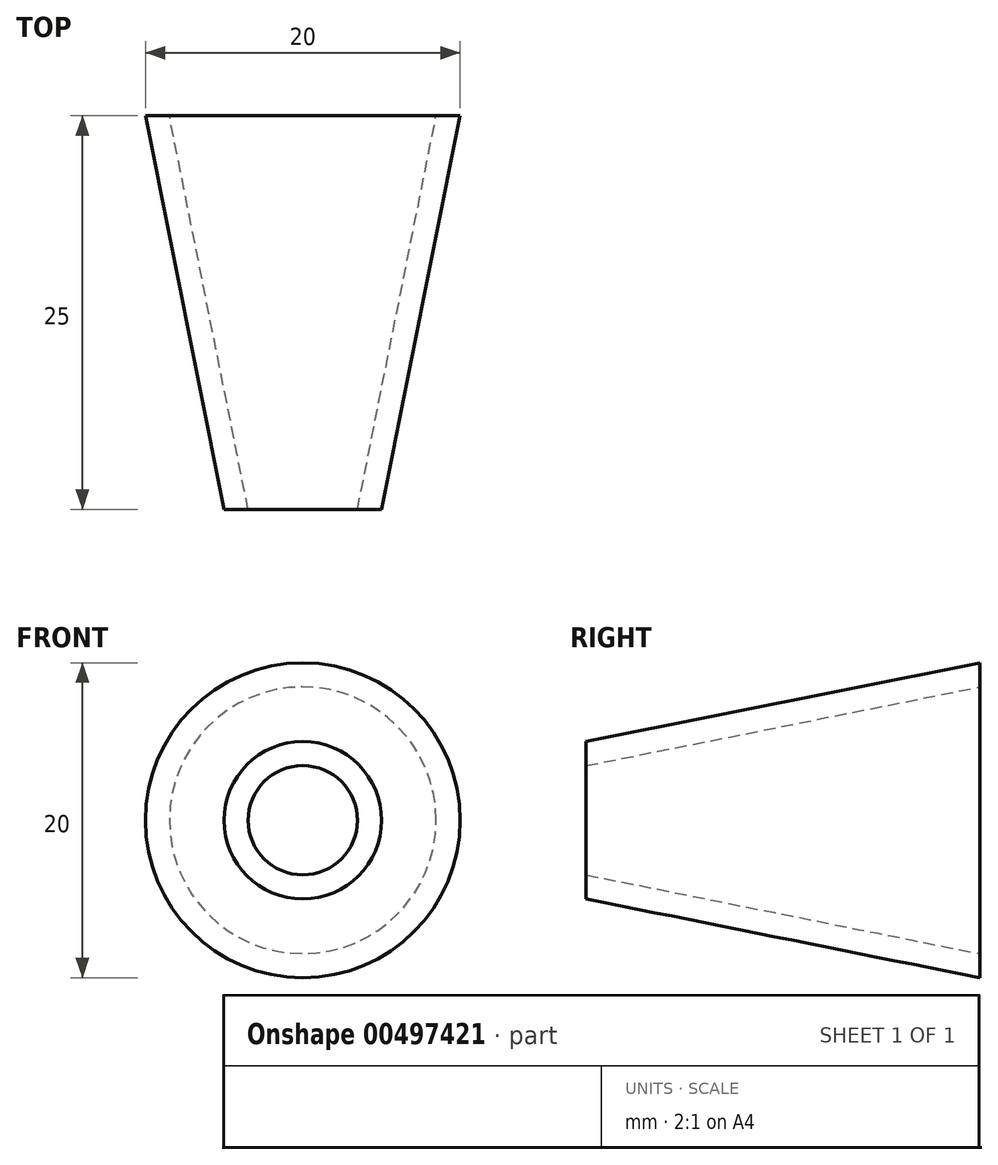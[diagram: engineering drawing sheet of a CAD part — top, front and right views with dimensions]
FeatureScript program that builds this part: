
annotation { "Feature Type Name" : "Feature", "Feature Type Description" : "" }
export const myFeature = defineFeature(function(context is Context, id is Id, definition is map)
    precondition{}
    {
        {
            var Q0;
            Q0=qCreatedBy(makeId("Front.planeOp"),FACE);
            var sketch = newSketch(context, id + "F0", { "sketchPlane" : qUnion([Q0])});
            skCircle(sketch, "E0", {"center": v(0, 0) * mm, "radius": 10 * mm});
            skSolve(sketch);
        }
        {
            var Q0;
            Q0 = qSketchRegion(id + "F0", true);
            extrude(context, id + "F1", {"entities" : qUnion([Q0]), "depth" : 25 * mm});
        }
        {
            var Q0;
            Q0=makeQuery(id+"F1.opExtrude","CAP_FACE",FACE,{"disambiguationData":[OSD([sQuery(id+"F0.wireOp",EDGE,"E0")])],"isStart":false});
            var sketch = newSketch(context, id + "F2", { "sketchPlane" : qUnion([Q0])});
            skCircle(sketch, "E1", {"center": v(0, 0) * mm, "radius": 5 * mm});
            skSolve(sketch);
        }
        {
            var Q1;
            Q1=makeQuery(id+"F1.opExtrude","CAP_FACE",FACE,{"disambiguationData":[OSD([sQuery(id+"F0.wireOp",EDGE,"E0")])],"isStart":true});
            var Q2;
            Q2=makeQuery(id+"F2.imprint","IMPRINT",FACE,{"disambiguationData":[TD([[makeQuery(id+"F2.imprint","IMPRINT",EDGE,{"derivedFrom":sQuery(id+"F2.wireOp",EDGE,"E1")}),1.0]])]});
            loft(context, id + "F3", {"operationType" : NewBodyOperationType.INTERSECT, "sheetProfilesArray" : [{ "sheetProfileEntities" : qUnion([Q1]) }, { "sheetProfileEntities" : qUnion([Q2]) }]});
        }
        {
            var Q0;
            Q0=makeQuery(id+"F1.opExtrude","CAP_FACE",FACE,{"disambiguationData":[OSD([sQuery(id+"F0.wireOp",EDGE,"E0")])],"isStart":true});
            var Q1;
            Q1=makeQuery(id+"F1.opExtrude","CAP_FACE",FACE,{"disambiguationData":[OSD([sQuery(id+"F0.wireOp",EDGE,"E0")])],"isStart":false});
            shell(context, id + "F4", {"entities" : qUnion([Q0, Q1]), "thickness" : 1.5 * mm});
        }
    });
